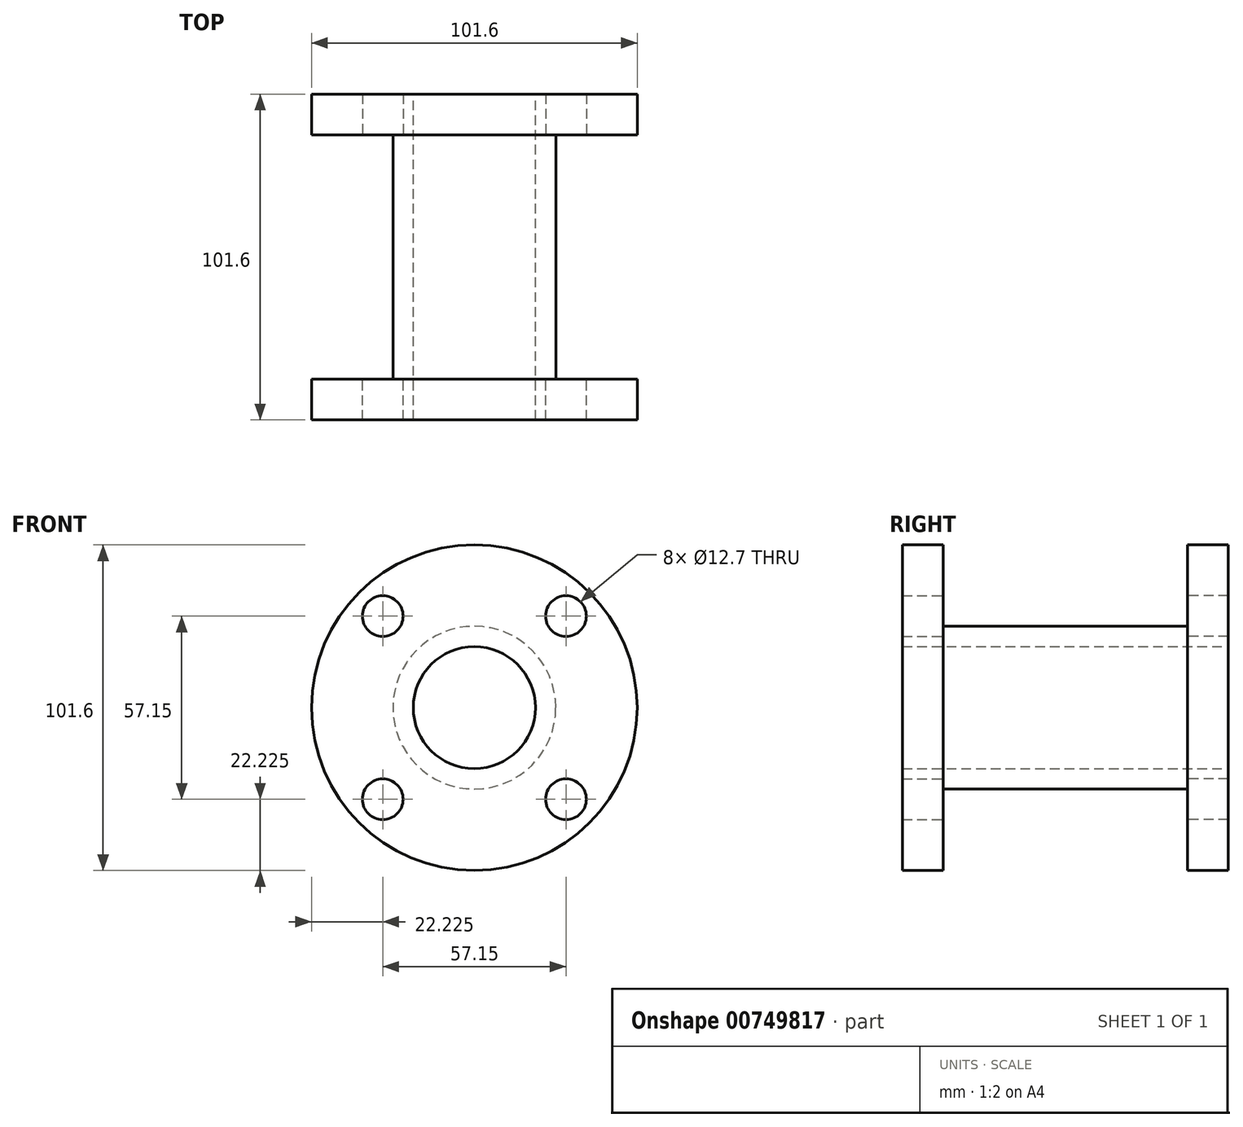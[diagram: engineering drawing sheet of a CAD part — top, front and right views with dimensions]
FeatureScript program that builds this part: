
annotation { "Feature Type Name" : "Feature", "Feature Type Description" : "" }
export const myFeature = defineFeature(function(context is Context, id is Id, definition is map)
    precondition{}
    {
        {
            var Q0;
            Q0=qCreatedBy(makeId("Front.planeOp"),FACE);
            var sketch = newSketch(context, id + "F0", { "sketchPlane" : qUnion([Q0])});
            skCircle(sketch, "E0", {"center": v(0, 0) * mm, "radius": 19.05 * mm});
            skCircle(sketch, "E1", {"center": v(0, 0) * mm, "radius": 50.8 * mm});
            skCircle(sketch, "E2", {"center": v(-28.58, 28.57) * mm, "radius": 6.35 * mm});
            skCircle(sketch, "E3", {"center": v(28.58, 28.58) * mm, "radius": 6.35 * mm});
            skCircle(sketch, "E4", {"center": v(-28.57, -28.58) * mm, "radius": 6.35 * mm});
            skCircle(sketch, "E5", {"center": v(28.58, -28.57) * mm, "radius": 6.35 * mm});
            skSolve(sketch);
        }
        {
            var Q0;
            Q0 = qSketchRegion(id + "F0", true);
            var Q1;
            Q1 = qSketchRegion(id + "F2", true);
            extrude(context, id + "F1", {"entities" : qUnion([Q0, Q1]), "depth" : 12.7 * mm, "offsetDistance" : 25.4 * mm});
        }
        {
            var Q0;
            Q0=makeQuery(id+"F1.opExtrude","CAP_FACE",FACE,{"disambiguationData":[OSD([sQuery(id+"F0.wireOp",EDGE,"E0"),sQuery(id+"F0.wireOp",EDGE,"E1"),sQuery(id+"F0.wireOp",EDGE,"E2"),sQuery(id+"F0.wireOp",EDGE,"E3"),sQuery(id+"F0.wireOp",EDGE,"E4"),sQuery(id+"F0.wireOp",EDGE,"E5")])],"isStart":true});
            var sketch = newSketch(context, id + "F2", { "sketchPlane" : qUnion([Q0])});
            skCircle(sketch, "E6", {"center": v(0, 0) * mm, "radius": 25.4 * mm});
            skSolve(sketch);
        }
        {
            var Q0;
            Q0 = qSketchRegion(id + "F2", true);
            extrude(context, id + "F3", {"entities" : qUnion([Q0]), "operationType" : NewBodyOperationType.ADD, "depth" : 76.2 * mm, "offsetDistance" : 25.4 * mm});
        }
        {
            var Q0;
            Q0=makeQuery(id+"F3.opExtrude","CAP_FACE",FACE,{"disambiguationData":[OSD([sQuery(id+"F2.wireOp",EDGE,"E6")])],"isStart":false});
            var sketch = newSketch(context, id + "F4", { "sketchPlane" : qUnion([Q0])});
            skCircle(sketch, "E7", {"center": v(0, 0) * mm, "radius": 50.8 * mm});
            skCircle(sketch, "E8", {"center": v(0, 0) * mm, "radius": 19.05 * mm});
            skCircle(sketch, "E9", {"center": v(-28.58, 28.57) * mm, "radius": 6.35 * mm});
            skCircle(sketch, "E10", {"center": v(28.58, 28.58) * mm, "radius": 6.35 * mm});
            skCircle(sketch, "E11", {"center": v(28.58, -28.57) * mm, "radius": 6.35 * mm});
            skCircle(sketch, "E12", {"center": v(-28.57, -28.58) * mm, "radius": 6.35 * mm});
            skSolve(sketch);
        }
        {
            var Q0;
            Q0 = qSketchRegion(id + "F4", true);
            extrude(context, id + "F5", {"entities" : qUnion([Q0]), "operationType" : NewBodyOperationType.ADD, "depth" : 12.7 * mm, "offsetDistance" : 25.4 * mm});
        }
        {
            var Q0;
            Q0=makeQuery(id+"F3.opExtrude","CAP_FACE",FACE,{"disambiguationData":[OSD([sQuery(id+"F2.wireOp",EDGE,"E6")])],"isStart":false});
            var sketch = newSketch(context, id + "F6", { "sketchPlane" : qUnion([Q0])});
            skCircle(sketch, "E13", {"center": v(0, 0) * mm, "radius": 19.05 * mm});
            skSolve(sketch);
        }
        {
            var Q0;
            Q0 = qSketchRegion(id + "F6", true);
            extrude(context, id + "F7", {"entities" : qUnion([Q0]), "operationType" : NewBodyOperationType.REMOVE, "oppositeDirection" : true, "depth" : 76.2 * mm, "offsetDistance" : 25.4 * mm});
        }
    });
